# Revit family: Lockin Lockers AU_Hanging Locker_R22
name_source: partatom
category: Furniture
units: mm (PartAtom-declared; Revit-internal decimal feet)

## family parameters
Always vertical = Yes
Cut with Voids When Loaded = No
OmniClass Number = 23.40.20.27
OmniClass Title = Storage Shelving
Render Appearance Source = Family Geometry
Room Calculation Point = No
Shared = Yes
Work Plane-Based = Yes

## types (11) — shared parameters
Body/Frame Material = Material - Melamine - Laminex or Polytec Finish
Depth Control = 500 mm  [stored 1.64042 ft]
Desired Depth = 500 mm  [stored 1.64042 ft]
Desired Height = 1900 mm  [stored 6.2336 ft]
Desired Width = 400 mm  [stored 1.31234 ft]
Door Material = Material - Melamine - Laminex or Polytec Finish
Height Control = 1900 mm  [stored 6.2336 ft]
Locker Joint = 3 mm  [stored 0.00984252 ft]
Manufacturer = Lockin Lockers AU
Maximum Depth = 600 mm
Maximum Height = 2100 mm
Maximum Width = 600 mm
Minimum Depth = 200 mm  [stored 0.656168 ft]
Minimum Height = 1800 mm  [stored 5.90551 ft]
Minimum Width = 300 mm
TH Wall = 18 mm  [stored 0.0590551 ft]
URL = https://www.lockin.com.au
Width Control = 400 mm  [stored 1.31234 ft]
vis_Shelf Bottom = Yes
zero-valued in all types: Default Elevation

## per-type parameters (varying)
| type | Base Height Control | Description | Desired Base Height | Door Type | H Locker | Height Shelf Offset Bottom | Height Shelf Offset Top | Maximum Base Height | Minimum Base Height | Model | N_Doors | Shoe Box Height | vis_2 Door | vis_Bench Seat | vis_Bench Seat & Shoe Box | vis_Bottom Cover Standard | vis_Coatrack Bottom | vis_Coatrack Top | vis_Floating Shelf Bottom | vis_Floating Shelf Top | vis_Full Width Shelf | vis_Shelf Top | vis_Shoe Box | vis_Wave Door |
| Hanging Locker 1 door (P1) | 100 mm  [stored 0.328084 ft] | Hanging Locker 1 door | 100 mm  [stored 0.328084 ft] | Lockin_Locker Door_R22 : Standard Door/Combination Lock | 1800 mm  [stored 5.90551 ft] | 898.5 mm  [stored 2.94783 ft] | 450 mm  [stored 1.47638 ft] | 200 mm  [stored 0.656168 ft] | 80 mm  [stored 0.262467 ft] | P1 | 1 | 0 mm  [stored 0 ft] | No | No | No | Yes | Yes | No | No | No | Yes | Yes | No | No |
| Hanging Locker 1 door w. floating shelf (PX1) | 100 mm  [stored 0.328084 ft] | Hanging Locker 1 door w. floating shelf | 100 mm  [stored 0.328084 ft] | Lockin_Locker Door_R22 : Standard Door/Combination Lock | 1800 mm  [stored 5.90551 ft] | 898.5 mm  [stored 2.94783 ft] | 450 mm  [stored 1.47638 ft] | 200 mm  [stored 0.656168 ft] | 80 mm  [stored 0.262467 ft] | PX1 | 1 | 0 mm  [stored 0 ft] | No | No | No | Yes | Yes | No | Yes | No | No | Yes | No | No |
| Hanging Locker 1 door w. bench seat (P1+) | 450 mm  [stored 1.47638 ft] | Hanging Locker 1 door w. bench seat | 450 mm  [stored 1.47638 ft] | Lockin_Locker Door_R22 : Standard Door/Combination Lock | 1450 mm  [stored 4.75722 ft] | 750 mm  [stored 2.46063 ft] | 300 mm | 450 mm  [stored 1.47638 ft] | 450 mm  [stored 1.47638 ft] | P1+ | 1 | 0 mm  [stored 0 ft] | No | Yes | No | Yes | Yes | No | No | No | Yes | Yes | No | No |
| Hanging Locker 2 door (P2) | 100 mm  [stored 0.328084 ft] | Hanging Locker 2 door | 100 mm  [stored 0.328084 ft] | Lockin_Locker Door_R22 : Standard Door/Combination Lock | 898.5 mm  [stored 2.94783 ft] | 880.5 mm  [stored 2.88878 ft] | 300 mm | 200 mm  [stored 0.656168 ft] | 80 mm  [stored 0.262467 ft] | P2 | 2 | 0 mm  [stored 0 ft] | Yes | No | No | Yes | Yes | Yes | No | No | Yes | No | No | No |
| Hanging Locker 2 door w. floating shelf (PX2) | 100 mm  [stored 0.328084 ft] | Hanging Locker 2 door w. floating shelf | 100 mm  [stored 0.328084 ft] | Lockin_Locker Door_R22 : Standard Door/Combination Lock | 898.5 mm  [stored 2.94783 ft] | 898.5 mm  [stored 2.94783 ft] | 300 mm | 200 mm  [stored 0.656168 ft] | 80 mm  [stored 0.262467 ft] | PX2 | 2 | 0 mm  [stored 0 ft] | Yes | No | No | Yes | No | No | Yes | Yes | No | No | No | No |
| Hanging Locker 2 door w. bench seat (P2+) | 450 mm  [stored 1.47638 ft] | Hanging Locker 2 door w. bench seat | 450 mm  [stored 1.47638 ft] | Lockin_Locker Door_R22 : Standard Door/Combination Lock | 723.5 mm  [stored 2.37369 ft] | 705.5 mm  [stored 2.31463 ft] | 300 mm | 450 mm  [stored 1.47638 ft] | 450 mm  [stored 1.47638 ft] | P2+ | 2 | 0 mm  [stored 0 ft] | Yes | Yes | No | Yes | Yes | Yes | No | No | Yes | No | No | No |
| Hanging Locker 2 door w. bench seat & shoe box (PS2) | 100 mm  [stored 0.328084 ft] | Hanging Locker 2 door w. bench seat & shoe box | 100 mm  [stored 0.328084 ft] | Lockin_Locker Door_R22 : Standard Door/Combination Lock | 723.5 mm  [stored 2.37369 ft] | 705.5 mm  [stored 2.31463 ft] | 300 mm | 200 mm  [stored 0.656168 ft] | 80 mm  [stored 0.262467 ft] | PS2 | 2 | 350 mm  [stored 1.14829 ft] | Yes | No | Yes | No | Yes | Yes | No | No | Yes | No | No | No |
| Hanging Locker 2 door w. shoe box (PB2) | 100 mm  [stored 0.328084 ft] | Hanging Locker 2 door w. shoe box | 100 mm  [stored 0.328084 ft] | Lockin_Locker Door_R22 : Standard Door/Combination Lock | 723.5 mm  [stored 2.37369 ft] | 705.5 mm  [stored 2.31463 ft] | 300 mm | 200 mm  [stored 0.656168 ft] | 80 mm  [stored 0.262467 ft] | PB2 | 2 | 350 mm  [stored 1.14829 ft] | Yes | No | No | Yes | Yes | Yes | No | No | Yes | No | Yes | No |
| Hanging Locker wave door (PL2) | 100 mm  [stored 0.328084 ft] | Hanging Locker wave door | 100 mm  [stored 0.328084 ft] | Lockin_Locker Door_R22 : Wave Door/OCS Lock | 1800 mm  [stored 5.90551 ft] | 300 mm | 300 mm | 200 mm  [stored 0.656168 ft] | 80 mm  [stored 0.262467 ft] | PL2 | 1 | 0 mm  [stored 0 ft] | No | No | No | Yes | No | No | No | No | Yes | Yes | No | Yes |
| Hanging Locker wave door w. bench seat & shoe box (PLS2) | 100 mm  [stored 0.328084 ft] | Hanging Locker wave door w. bench seat & shoe box | 100 mm  [stored 0.328084 ft] | Lockin_Locker Door_R22 : Wave Door/OCS Lock | 1450 mm  [stored 4.75722 ft] | 300 mm | 300 mm | 200 mm  [stored 0.656168 ft] | 80 mm  [stored 0.262467 ft] | PLS2 | 1 | 350 mm  [stored 1.14829 ft] | No | No | Yes | No | Yes | Yes | No | Yes | Yes | Yes | No | Yes |
| Hanging Locker wave door w. shoe box (PLB) | 100 mm  [stored 0.328084 ft] | Hanging Locker wave door w. shoe box | 100 mm  [stored 0.328084 ft] | Lockin_Locker Door_R22 : Wave Door/OCS Lock | 1450 mm  [stored 4.75722 ft] | 300 mm | 300 mm | 200 mm  [stored 0.656168 ft] | 80 mm  [stored 0.262467 ft] | PLB | 1 | 350 mm  [stored 1.14829 ft] | No | No | No | Yes | Yes | Yes | No | Yes | Yes | Yes | Yes | Yes |

note: [stored X ft] marks values corroborated as IEEE doubles in the binary element streams (Revit-internal decimal feet)

## geometry (parser evidence)
native form markers: Sweep x6
no freeform markers — native parametric forms only
